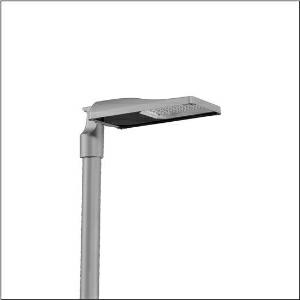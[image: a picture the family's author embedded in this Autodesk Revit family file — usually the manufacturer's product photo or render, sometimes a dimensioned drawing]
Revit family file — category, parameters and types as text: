
# Revit family: streetlight_sl_31_mini___p1_0a_5xh2a5aa08ha_a734
name_source: partatom
category: Lighting Fixtures
units: mm (PartAtom-declared; Revit-internal decimal feet)

## family parameters
Cut with Voids When Loaded = No
Host = Face
Light Source = No
Part Type = Normal
Room Calculation Point = No
Round Connector Dimension = Use Diameter
Shared = No

## types (1)
- --- (1 x LED, 7880 lm, 68.3 W, 3000K)
    Apparent Load = 68 VA
    CIE Flux Codes = 23 55 94 100 100
    Color Rendering = 80
    Color Temperature = 3000K
    Default Elevation = 1800 mm
    Description = Streetlight SL 31 mini Easy mast luminaire for post-top, side-entry; light control with lens of PMMA; light distribution: P1.0a, direct asymmetric distribution, for standard-compliant lighting for roads and squares; LED: luminous flux: 7.880lm, light colour: 830, colour temperature: 3000K; luminous efficacy: 115,4lm/W; control: overheat protection, intelligent temperature release in ECG and LED module, constant luminous flux control, time-dependent luminous flux control, flexible luminous flux parameterisation, pre-setting: linear dimming characteristic; luminaire housing, of diecast aluminium, SITECO metallic grey (DB 702S), corrosivity category C5 high according to DIN EN ISO 12944; cover of toughened safety glass, transparent, mast flange of diecast aluminium, SITECO metallic grey (DB 702S), spigot size: 76/60mm, mast flange included unmounted; with cable H07RN-F 2x 1.5mm², cable length: 8,5m, connection cable pre-assembled; mains connection: 220..240V, AC, 50/60Hz; power consumption (at start of service life): 68,3W / (at end of service life): 74,8W / (with reduced operation 50%): 29,4W; protection rating (complete): IP66; insulation class (complete): insulation class II (safety insulation); impact resistance: IK10; certification: CE, ENEC, ENEC+, VDE, UKCA; permissible operating ambient temperature for outdoor applications: -40..+50°C; packaging unit: 1 piece

Light Distribution: P1.0a
    Height = 76 mm
    Lamp = 1 x LED
    Lamp Light Flux = 7880 lm
    Lamp Power = 68.3 W
    Lamp count = 1
    Length = 547 mm
    Luminous efficacy = 115 lm/W
    Manufacturer = Siteco
    ModVariant = No
    Model = 5XH2A5AA08HA
    Number of Poles = 1
    OnlyDefault = Yes
    Power Factor = 1
    Product Name = Streetlight SL 31 mini | P1.0a
    Product group = mast luminaire | pylon top
    ProductGroupID = 6100
    Protection Class = Protection class II
    Protection Degree = IP 66
    RLX_Detail_Level = 1
    RLX_Emergency_Light_Flux = 0 lm
    RLX_Emergency_Type = 0
    RLX_Emergency_Type_DB = No
    RlxData = <blob elided: 39121 chars, md5=6e8fd22c>
    Socket = socket
    Standby Power = 0 W
    System Light Flux = 7880 lm
    System Power = 68 W
    Type Comments = factory setting: luminous flux: 100 % | dim-lin: 254 | 693 mA
    Type Image = l_1300326.jpg
    URL = http://relux.com
    VarID = @adj_064733
    Voltage = 0 V
    Weight = 0.00 kg
    Width = 265 mm

## geometry (parser evidence)
native form markers: Blend x4, Sweep x9
no freeform markers — native parametric forms only
